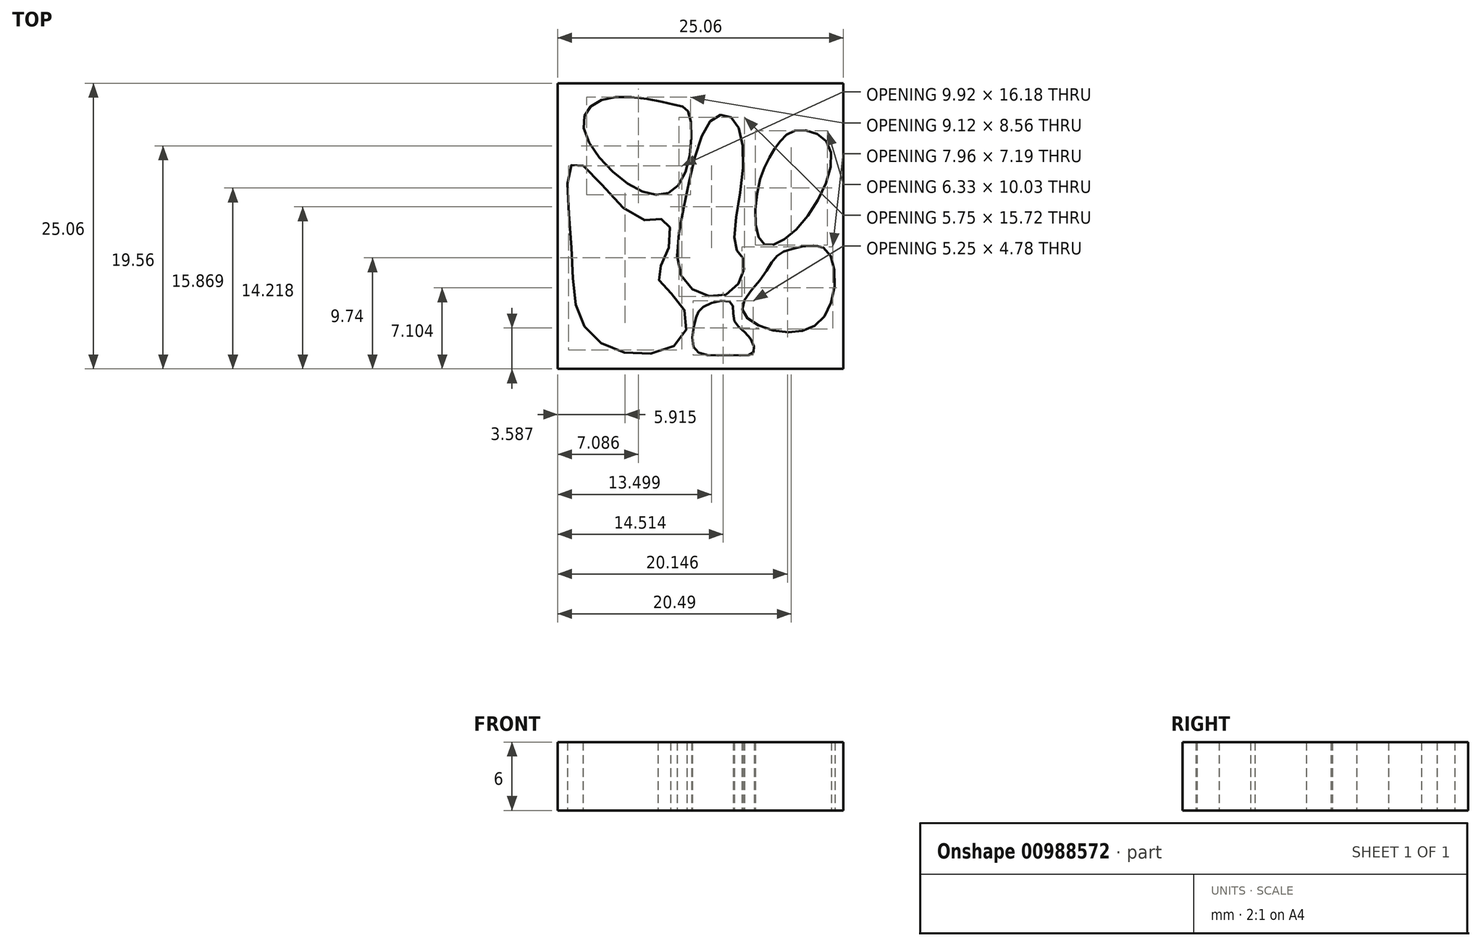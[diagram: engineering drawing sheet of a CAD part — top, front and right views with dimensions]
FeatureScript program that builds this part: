
annotation { "Feature Type Name" : "Feature", "Feature Type Description" : "" }
export const myFeature = defineFeature(function(context is Context, id is Id, definition is map)
    precondition{}
    {
        {
            var Q0;
            Q0=qCreatedBy(makeId("Top.planeOp"),FACE);
            var sketch = newSketch(context, id + "F0", { "sketchPlane" : qUnion([Q0])});
            skLineSegment(sketch, "E0.bottom", {"start": v(-56.23, 20.73) * mm, "end": v(-31.17, 20.73) * mm});
            skLineSegment(sketch, "E0.top", {"start": v(-56.23, -4.33) * mm, "end": v(-31.17, -4.33) * mm});
            skLineSegment(sketch, "E0.left", {"start": v(-56.23, 20.73) * mm, "end": v(-56.23, -4.33) * mm});
            skLineSegment(sketch, "E0.right", {"start": v(-31.17, 20.73) * mm, "end": v(-31.17, -4.33) * mm});
            skSolve(sketch);
        }
        {
            var Q0;
            Q0=makeQuery(id+"F0.imprint","IMPRINT",FACE,{"disambiguationData":[TD([[makeQuery(id+"F0.imprint","IMPRINT",EDGE,{"derivedFrom":sQuery(id+"F0.wireOp",EDGE,"E0.bottom")}),-1.0]])]});
            extrude(context, id + "F1", {"entities" : qUnion([Q0]), "depth" : 6 * mm, "offsetDistance" : 25 * mm});
        }
        {
            var Q0;
            Q0=makeQuery(id+"F1.opExtrude","CAP_FACE",FACE,{"disambiguationData":[OSD([sQuery(id+"F0.wireOp",EDGE,"E0.bottom"),sQuery(id+"F0.wireOp",EDGE,"E0.top"),sQuery(id+"F0.wireOp",EDGE,"E0.left"),sQuery(id+"F0.wireOp",EDGE,"E0.right")])],"isStart":false});
            var sketch = newSketch(context, id + "F2", { "sketchPlane" : qUnion([Q0])});
            skFitSpline(sketch, "E1", {"points": [v(-35.42, 16.56) * mm, v(-37.14, 15.06) * mm, v(-38.63, 11.7) * mm, v(-38.26, 6.71) * mm, v(-34.83, 8.43) * mm, v(-32.44, 15.29) * mm, v(-35.42, 16.56) * mm]});
            skSolve(sketch);
        }
        {
            var Q0;
            Q0 = qSketchRegion(id + "F2", true);
            extrude(context, id + "F3", {"entities" : qUnion([Q0]), "operationType" : NewBodyOperationType.REMOVE, "oppositeDirection" : true, "depth" : 25 * mm, "offsetDistance" : 25 * mm});
        }
        {
            var Q0;
            Q0=makeQuery(id+"F1.opExtrude","CAP_FACE",FACE,{"disambiguationData":[OSD([sQuery(id+"F0.wireOp",EDGE,"E0.bottom"),sQuery(id+"F0.wireOp",EDGE,"E0.top"),sQuery(id+"F0.wireOp",EDGE,"E0.left"),sQuery(id+"F0.wireOp",EDGE,"E0.right")])],"isStart":false});
            var sketch = newSketch(context, id + "F4", { "sketchPlane" : qUnion([Q0])});
            skFitSpline(sketch, "E2", {"points": [v(-41.02, 17.75) * mm, v(-39.97, 13.42) * mm, v(-40.64, 6.34) * mm, v(-39.9, 5.15) * mm, v(-41.24, 2.31) * mm, v(-45.12, 3.36) * mm, v(-44.97, 10.81) * mm, v(-42.73, 17.52) * mm, v(-41.02, 17.75) * mm]});
            skSolve(sketch);
        }
        {
            var Q0;
            Q0=makeQuery(id+"F4.imprint","IMPRINT",FACE,{"disambiguationData":[TD([[makeQuery(id+"F4.imprint","IMPRINT",EDGE,{"derivedFrom":sQuery(id+"F4.wireOp",EDGE,"E2")}),-1.0]])]});
            extrude(context, id + "F5", {"entities" : qUnion([Q0]), "operationType" : NewBodyOperationType.REMOVE, "oppositeDirection" : true, "depth" : 25 * mm, "offsetDistance" : 25 * mm});
        }
        {
            var Q0;
            Q0=makeQuery(id+"F1.opExtrude","CAP_FACE",FACE,{"disambiguationData":[OSD([sQuery(id+"F0.wireOp",EDGE,"E0.bottom"),sQuery(id+"F0.wireOp",EDGE,"E0.top"),sQuery(id+"F0.wireOp",EDGE,"E0.left"),sQuery(id+"F0.wireOp",EDGE,"E0.right")])],"isStart":false});
            var sketch = newSketch(context, id + "F6", { "sketchPlane" : qUnion([Q0])});
            skFitSpline(sketch, "E3", {"points": [v(-36.99, 5.6) * mm, v(-38.4, 3.58) * mm, v(-40.05, 0.82) * mm, v(-36.32, -1.12) * mm, v(-32.51, 0.82) * mm, v(-32.66, 6.12) * mm, v(-35.35, 6.26) * mm, v(-36.99, 5.6) * mm]});
            skSolve(sketch);
        }
        {
            var Q0;
            Q0=makeQuery(id+"F6.imprint","IMPRINT",FACE,{"disambiguationData":[TD([[makeQuery(id+"F6.imprint","IMPRINT",EDGE,{"derivedFrom":sQuery(id+"F6.wireOp",EDGE,"E3")}),1.0]])]});
            extrude(context, id + "F7", {"entities" : qUnion([Q0]), "operationType" : NewBodyOperationType.REMOVE, "oppositeDirection" : true, "depth" : 25 * mm, "offsetDistance" : 25 * mm});
        }
        {
            var Q0;
            Q0=makeQuery(id+"F1.opExtrude","CAP_FACE",FACE,{"disambiguationData":[OSD([sQuery(id+"F0.wireOp",EDGE,"E0.bottom"),sQuery(id+"F0.wireOp",EDGE,"E0.top"),sQuery(id+"F0.wireOp",EDGE,"E0.left"),sQuery(id+"F0.wireOp",EDGE,"E0.right")])],"isStart":false});
            var sketch = newSketch(context, id + "F8", { "sketchPlane" : qUnion([Q0])});
            skFitSpline(sketch, "E4", {"points": [v(-46.01, 18.87) * mm, v(-51.6, 19.46) * mm, v(-54, 17.15) * mm, v(-49.22, 11.4) * mm, v(-45.5, 12) * mm, v(-44.74, 18.12) * mm, v(-46.01, 18.87) * mm]});
            skSolve(sketch);
        }
        {
            var Q0;
            Q0=makeQuery(id+"F8.imprint","IMPRINT",FACE,{"disambiguationData":[TD([[makeQuery(id+"F8.imprint","IMPRINT",EDGE,{"derivedFrom":sQuery(id+"F8.wireOp",EDGE,"E4")}),1.0]])]});
            extrude(context, id + "F9", {"entities" : qUnion([Q0]), "operationType" : NewBodyOperationType.REMOVE, "oppositeDirection" : true, "depth" : 25 * mm, "offsetDistance" : 25 * mm});
        }
        {
            var Q0;
            Q0=makeQuery(id+"F1.opExtrude","CAP_FACE",FACE,{"disambiguationData":[OSD([sQuery(id+"F0.wireOp",EDGE,"E0.bottom"),sQuery(id+"F0.wireOp",EDGE,"E0.top"),sQuery(id+"F0.wireOp",EDGE,"E0.left"),sQuery(id+"F0.wireOp",EDGE,"E0.right")])],"isStart":false});
            var sketch = newSketch(context, id + "F10", { "sketchPlane" : qUnion([Q0])});
            skFitSpline(sketch, "E5", {"points": [v(-54, 13.5) * mm, v(-49, 8.8) * mm, v(-46.76, 8.73) * mm, v(-46.53, 6.12) * mm, v(-47.43, 3.65) * mm, v(-45.34, 1.27) * mm, v(-45.5, -1.86) * mm, v(-50.41, -2.9) * mm, v(-54.22, 0) * mm, v(-55.04, 6.49) * mm, v(-55.11, 13.42) * mm, v(-54, 13.5) * mm]});
            skSolve(sketch);
        }
        {
            var Q0;
            Q0=makeQuery(id+"F10.imprint","IMPRINT",FACE,{"disambiguationData":[TD([[makeQuery(id+"F10.imprint","IMPRINT",EDGE,{"derivedFrom":sQuery(id+"F10.wireOp",EDGE,"E5")}),-1.0]])]});
            extrude(context, id + "F11", {"entities" : qUnion([Q0]), "operationType" : NewBodyOperationType.REMOVE, "oppositeDirection" : true, "depth" : 25 * mm, "offsetDistance" : 25 * mm});
        }
        {
            var Q0;
            Q0=makeQuery(id+"F1.opExtrude","CAP_FACE",FACE,{"disambiguationData":[OSD([sQuery(id+"F0.wireOp",EDGE,"E0.bottom"),sQuery(id+"F0.wireOp",EDGE,"E0.top"),sQuery(id+"F0.wireOp",EDGE,"E0.left"),sQuery(id+"F0.wireOp",EDGE,"E0.right")])],"isStart":false});
            var sketch = newSketch(context, id + "F12", { "sketchPlane" : qUnion([Q0])});
            skFitSpline(sketch, "E6", {"points": [v(-41.16, -3.13) * mm, v(-44.15, -2.68) * mm, v(-44.15, 0) * mm, v(-43.33, 1.2) * mm, v(-41.02, 1.5) * mm, v(-40.8, 0) * mm, v(-39.52, -1.42) * mm, v(-39.08, -2.9) * mm, v(-41.16, -3.13) * mm]});
            skSolve(sketch);
        }
        {
            var Q0;
            Q0=makeQuery(id+"F12.imprint","IMPRINT",FACE,{"disambiguationData":[TD([[makeQuery(id+"F12.imprint","IMPRINT",EDGE,{"derivedFrom":sQuery(id+"F12.wireOp",EDGE,"E6")}),-1.0]])]});
            extrude(context, id + "F13", {"entities" : qUnion([Q0]), "operationType" : NewBodyOperationType.REMOVE, "oppositeDirection" : true, "depth" : 25 * mm, "offsetDistance" : 25 * mm});
        }
    });
